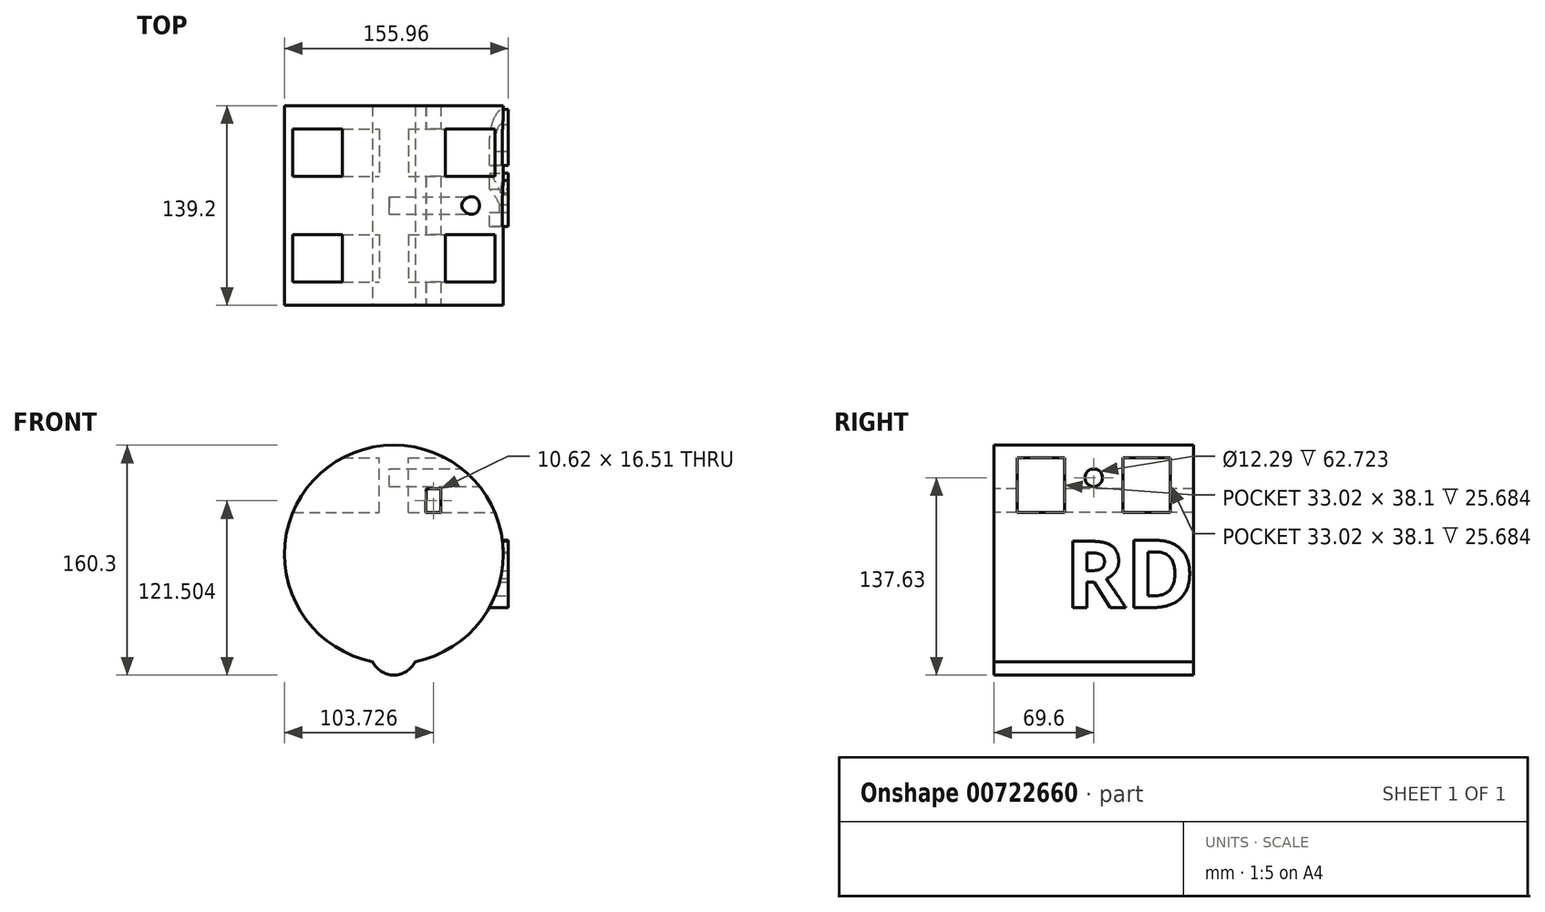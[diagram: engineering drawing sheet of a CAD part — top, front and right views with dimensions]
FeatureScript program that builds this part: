
annotation { "Feature Type Name" : "Feature", "Feature Type Description" : "" }
export const myFeature = defineFeature(function(context is Context, id is Id, definition is map)
    precondition{}
    {
        {
            var Q0;
            Q0=qCreatedBy(makeId("Front.planeOp"),FACE);
            var sketch = newSketch(context, id + "F0", { "sketchPlane" : qUnion([Q0])});
            skCircle(sketch, "E0", {"center": v(0, 0) * mm, "radius": 76.2 * mm});
            skSolve(sketch);
        }
        {
            var Q0;
            Q0=makeQuery(id+"F0.imprint","IMPRINT",FACE,{"disambiguationData":[TD([[makeQuery(id+"F0.imprint","IMPRINT",EDGE,{"derivedFrom":sQuery(id+"F0.wireOp",EDGE,"E0")}),1.0]])]});
            extrude(context, id + "F1", {"entities" : qUnion([Q0]), "endBound" : BoundingType.SYMMETRIC, "depth" : 139.2 * mm, "offsetDistance" : 25.4 * mm});
        }
        {
            var Q0;
            Q0=qCreatedBy(makeId("Right.planeOp"),FACE);
            cPlane(context, id + "F2", {"entities" : qUnion([Q0]), "cplaneType" : CPlaneType.OFFSET, "offset" : 79.76 * mm, "width" : 152.4 * mm, "height" : 152.4 * mm});
        }
        {
            var Q0;
            Q0=qCreatedBy(id+"F2.planeOp",FACE);
            var sketch = newSketch(context, id + "F3", { "sketchPlane" : qUnion([Q0])});
            skLineSegment(sketch, "E1", {"start": v(0, 65.02) * mm, "end": v(0, 36.36) * mm});
            skLineSegment(sketch, "E2.bottom", {"start": v(-53.34, 67.25) * mm, "end": v(-20.32, 67.25) * mm});
            skLineSegment(sketch, "E2.top", {"start": v(-53.34, 29.15) * mm, "end": v(-20.32, 29.15) * mm});
            skLineSegment(sketch, "E2.left", {"start": v(-53.34, 67.25) * mm, "end": v(-53.34, 29.15) * mm});
            skLineSegment(sketch, "E2.right", {"start": v(-20.32, 67.25) * mm, "end": v(-20.32, 29.15) * mm});
            skPoint(sketch, "E2.middle", {"position": v(-36.83, 48.2) * mm});
            skLineSegment(sketch, "E3.bottom", {"start": v(20.32, 67.25) * mm, "end": v(53.34, 67.25) * mm});
            skLineSegment(sketch, "E3.top", {"start": v(20.32, 29.15) * mm, "end": v(53.34, 29.15) * mm});
            skLineSegment(sketch, "E3.left", {"start": v(20.32, 67.25) * mm, "end": v(20.32, 29.15) * mm});
            skLineSegment(sketch, "E3.right", {"start": v(53.34, 67.25) * mm, "end": v(53.34, 29.15) * mm});
            skPoint(sketch, "E3.middle", {"position": v(36.83, 48.2) * mm});
            skSolve(sketch);
        }
        {
            var Q0;
            Q0=makeQuery(id+"F3.imprint","IMPRINT",FACE,{"disambiguationData":[TD([[makeQuery(id+"F3.imprint","IMPRINT",EDGE,{"derivedFrom":sQuery(id+"F3.wireOp",EDGE,"E2.bottom")}),-1.0]])]});
            var Q1;
            Q1=makeQuery(id+"F3.imprint","IMPRINT",FACE,{"disambiguationData":[TD([[makeQuery(id+"F3.imprint","IMPRINT",EDGE,{"derivedFrom":sQuery(id+"F3.wireOp",EDGE,"E3.bottom")}),-1.0]])]});
            extrude(context, id + "F4", {"entities" : qUnion([Q0, Q1]), "operationType" : NewBodyOperationType.REMOVE, "oppositeDirection" : true, "depth" : 170.43 * mm, "offsetDistance" : 25.4 * mm});
        }
        {
            var Q0;
            Q0=makeQuery(id+"F1.opExtrude","CAP_FACE",FACE,{"disambiguationData":[OSD([sQuery(id+"F0.wireOp",EDGE,"E0")])],"isStart":true});
            var sketch = newSketch(context, id + "F5", { "sketchPlane" : qUnion([Q0])});
            skLineSegment(sketch, "E4.bottom", {"start": v(-10.15, 75.52) * mm, "end": v(10.15, 75.52) * mm});
            skLineSegment(sketch, "E4.top", {"start": v(-10.15, 13.3) * mm, "end": v(10.15, 13.3) * mm});
            skLineSegment(sketch, "E4.left", {"start": v(-10.15, 75.52) * mm, "end": v(-10.15, 13.3) * mm});
            skLineSegment(sketch, "E4.right", {"start": v(10.15, 75.52) * mm, "end": v(10.15, 13.3) * mm});
            skPoint(sketch, "E4.middle", {"position": v(0, 44.4) * mm});
            skSolve(sketch);
        }
        {
            var Q0;
            {var subQ0=sQuery(id+"F5.wireOp",EDGE,"E4.bottom");Q0=makeQuery(id+"F5.imprint","IMPRINT",FACE,{"disambiguationData":[TD([[makeQuery(id+"F5.imprint","IMPRINT",EDGE,{"derivedFrom":subQ0}),-1.0]])]});}
            extrude(context, id + "F6", {"entities" : qUnion([Q0]), "operationType" : NewBodyOperationType.ADD, "oppositeDirection" : true, "depth" : 135.13 * mm, "offsetDistance" : 25.4 * mm});
        }
        {
            var Q0;
            Q0=qCreatedBy(makeId("Front.planeOp"),FACE);
            var sketch = newSketch(context, id + "F7", { "sketchPlane" : qUnion([Q0])});
            skCircle(sketch, "E5", {"center": v(0, -67.74) * mm, "radius": 16.35 * mm});
            skSolve(sketch);
        }
        {
            var Q0;
            Q0=makeQuery(id+"F7.imprint","IMPRINT",FACE,{"disambiguationData":[TD([[makeQuery(id+"F7.imprint","IMPRINT",EDGE,{"derivedFrom":sQuery(id+"F7.wireOp",EDGE,"E5")}),1.0]])]});
            extrude(context, id + "F8", {"entities" : qUnion([Q0]), "operationType" : NewBodyOperationType.ADD, "endBound" : BoundingType.SYMMETRIC, "oppositeDirection" : true, "depth" : 139.2 * mm, "offsetDistance" : 25.4 * mm});
        }
        {
            var Q0;
            Q0=makeQuery(id+"F6.boolean.opBoolean","SPLIT",FACE,{"disambiguationData":[TD([makeQuery(id+"F6.opExtrude","SWEPT_FACE",FACE,{"disambiguationData":[OSD([sQuery(id+"F5.wireOp",EDGE,"E4.left")])]})])],"derivedFrom":makeQuery(id+"F4.boolean.opBoolean","COPY",FACE,{"derivedFrom":makeQuery(id+"F4.opExtrude","SWEPT_FACE",FACE,{"disambiguationData":[OSD([sQuery(id+"F3.wireOp",EDGE,"E2.left")])]})})});
            var sketch = newSketch(context, id + "F9", { "sketchPlane" : qUnion([Q0])});
            skLineSegment(sketch, "E6", {"start": v(-32.84, 29.15) * mm, "end": v(-32.84, 45.66) * mm});
            skLineSegment(sketch, "E7", {"start": v(-32.84, 45.66) * mm, "end": v(-22.68, 45.66) * mm});
            skLineSegment(sketch, "E8", {"start": v(-22.68, 45.66) * mm, "end": v(-22.22, 29.15) * mm});
            skLineSegment(sketch, "E9", {"start": v(-22.22, 29.15) * mm, "end": v(-32.84, 29.15) * mm});
            skSolve(sketch);
        }
        {
            var Q0;
            Q0=makeQuery(id+"F9.imprint","IMPRINT",FACE,{"disambiguationData":[TD([[makeQuery(id+"F9.imprint","IMPRINT",EDGE,{"derivedFrom":sQuery(id+"F9.wireOp",EDGE,"E6")}),-1.0]])]});
            extrude(context, id + "F10", {"entities" : qUnion([Q0]), "operationType" : NewBodyOperationType.REMOVE, "endBound" : BoundingType.SYMMETRIC, "depth" : 273.3 * mm, "offsetDistance" : 25.4 * mm});
        }
        {
            var Q0;
            Q0=qCreatedBy(id+"F2.planeOp",FACE);
            var sketch = newSketch(context, id + "F11", { "sketchPlane" : qUnion([Q0])});
            skText(sketch, "E10", { "text": "D", "fontName": "OpenSans-Bold.ttf"});
            const initialGuessF11  = {"E10": [0.022, -0.03702, 1, 0, 0.04735]};
            skSetInitialGuess(sketch, initialGuessF11);
            skSolve(sketch);
        }
        {
            var Q0;
            Q0=makeQuery(id+"F11.imprint","IMPRINT",FACE,{"disambiguationData":[TD([[makeQuery(id+"F11.imprint","IMPRINT",EDGE,{"derivedFrom":sQuery(id+"F11.wireOp",EDGE,"E10.sketch_text.stroke-0")}),-1.0]])]});
            extrude(context, id + "F12", {"entities" : qUnion([Q0]), "operationType" : NewBodyOperationType.ADD, "oppositeDirection" : true, "depth" : 25.9 * mm, "offsetDistance" : 25.4 * mm});
        }
        {
            var Q0;
            Q0=qCreatedBy(id+"F2.planeOp",FACE);
            var sketch = newSketch(context, id + "F13", { "sketchPlane" : qUnion([Q0])});
            skText(sketch, "E11", { "text": "R", "fontName": "OpenSans-Bold.ttf"});
            const initialGuessF13  = {"E11": [-0.02032, -0.03702, 1, 0, 0.04658]};
            skSetInitialGuess(sketch, initialGuessF13);
            skSolve(sketch);
        }
        {
            var Q0;
            Q0=makeQuery(id+"F13.imprint","IMPRINT",FACE,{"disambiguationData":[TD([[makeQuery(id+"F13.imprint","IMPRINT",EDGE,{"derivedFrom":sQuery(id+"F13.wireOp",EDGE,"E11.sketch_text.stroke-0")}),-1.0]])]});
            extrude(context, id + "F14", {"entities" : qUnion([Q0]), "operationType" : NewBodyOperationType.ADD, "oppositeDirection" : true, "depth" : 13.97 * mm, "offsetDistance" : 25.4 * mm});
        }
        {
            var Q0;
            Q0=qCreatedBy(id+"F2.planeOp",FACE);
            var sketch = newSketch(context, id + "F15", { "sketchPlane" : qUnion([Q0])});
            skCircle(sketch, "E12", {"center": v(0, 53.53) * mm, "radius": 6.15 * mm});
            skSolve(sketch);
        }
        {
            var Q0;
            Q0=makeQuery(id+"F15.imprint","IMPRINT",FACE,{"disambiguationData":[TD([[makeQuery(id+"F15.imprint","IMPRINT",EDGE,{"derivedFrom":sQuery(id+"F15.wireOp",EDGE,"E12")}),1.0]])]});
            var Q1;
            Q1=sQuery(id+"F15.wireOp",EDGE,"E12");
            extrude(context, id + "F16", {"entities" : qUnion([Q0]), "operationType" : NewBodyOperationType.REMOVE, "surfaceEntities" : qUnion([Q1]), "oppositeDirection" : true, "depth" : 82.8 * mm, "offsetDistance" : 25.4 * mm});
        }
    });
